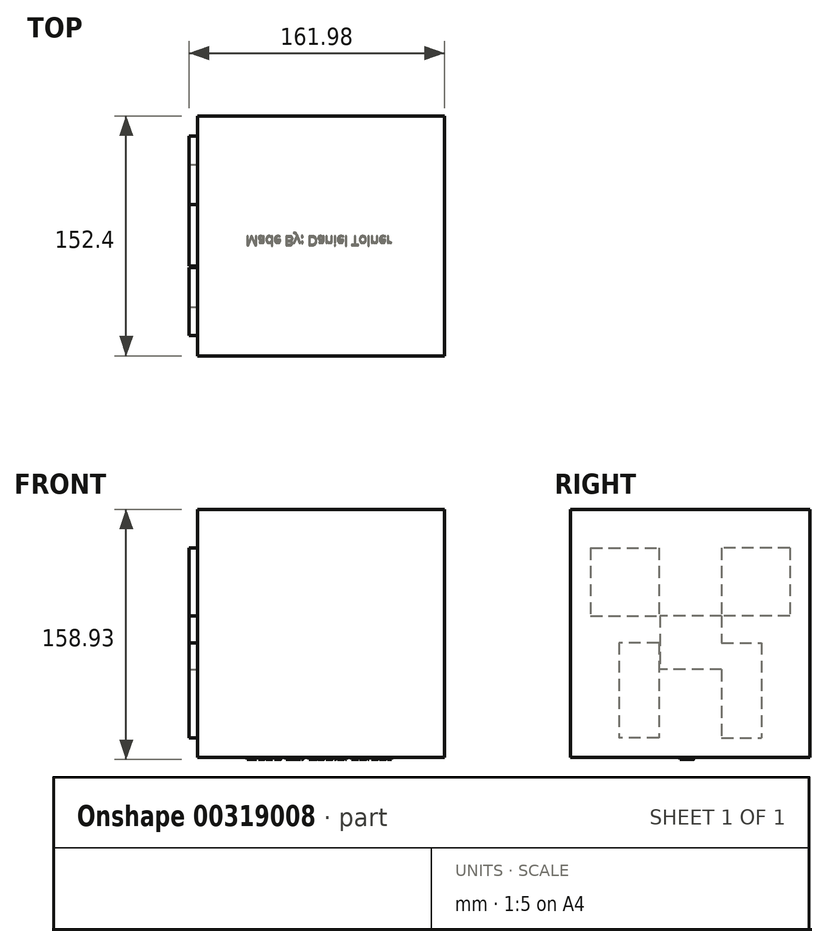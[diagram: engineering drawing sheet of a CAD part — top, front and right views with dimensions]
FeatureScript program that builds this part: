
annotation { "Feature Type Name" : "Feature", "Feature Type Description" : "" }
export const myFeature = defineFeature(function(context is Context, id is Id, definition is map)
    precondition{}
    {
        {
            var Q0;
            Q0=qCreatedBy(makeId("Front.planeOp"),FACE);
            var sketch = newSketch(context, id + "F0", { "sketchPlane" : qUnion([Q0])});
            skLineSegment(sketch, "E0.bottom", {"start": v(-81, -82.02) * mm, "end": v(75.64, -82.02) * mm});
            skLineSegment(sketch, "E0.top", {"start": v(-81, 75.64) * mm, "end": v(75.64, 75.64) * mm});
            skLineSegment(sketch, "E0.left", {"start": v(-81, -82.02) * mm, "end": v(-81, 75.64) * mm});
            skLineSegment(sketch, "E0.right", {"start": v(75.64, -82.02) * mm, "end": v(75.64, 75.64) * mm});
            skSolve(sketch);
        }
        {
            var Q0;
            Q0=makeQuery(id+"F0.imprint","IMPRINT",FACE,{"disambiguationData":[TD([[makeQuery(id+"F0.imprint","IMPRINT",EDGE,{"derivedFrom":sQuery(id+"F0.wireOp",EDGE,"E0.bottom")}),1.0]])]});
            extrude(context, id + "F1", {"entities" : qUnion([Q0]), "endBound" : BoundingType.SYMMETRIC, "depth" : 152.4 * mm});
        }
        {
            var Q0;
            Q0=makeQuery(id+"F1.opExtrude","SWEPT_FACE",FACE,{"disambiguationData":[OSD([sQuery(id+"F0.wireOp",EDGE,"E0.left")])]});
            var sketch = newSketch(context, id + "F2", { "sketchPlane" : qUnion([Q0])});
            skLineSegment(sketch, "E1.bottom", {"start": v(-63.3, 51.08) * mm, "end": v(-19.95, 51.08) * mm});
            skLineSegment(sketch, "E1.top", {"start": v(-63.3, 8.01) * mm, "end": v(-19.95, 8.01) * mm});
            skLineSegment(sketch, "E1.left", {"start": v(-63.3, 51.08) * mm, "end": v(-63.3, 8.01) * mm});
            skLineSegment(sketch, "E1.right", {"start": v(-19.95, 51.08) * mm, "end": v(-19.95, 8.01) * mm});
            skLineSegment(sketch, "E2.bottom", {"start": v(-19.95, 8.01) * mm, "end": v(19.3, 8.01) * mm});
            skLineSegment(sketch, "E2.top", {"start": v(-19.95, -26.17) * mm, "end": v(19.3, -26.17) * mm});
            skLineSegment(sketch, "E2.left", {"start": v(-19.95, 8.01) * mm, "end": v(-19.95, -26.17) * mm});
            skLineSegment(sketch, "E2.right", {"start": v(19.3, 8.01) * mm, "end": v(19.3, -26.17) * mm});
            skLineSegment(sketch, "E3.bottom", {"start": v(-19.95, -9.08) * mm, "end": v(-45.28, -9.08) * mm});
            skLineSegment(sketch, "E3.top", {"start": v(-19.95, -69.55) * mm, "end": v(-45.28, -69.55) * mm});
            skLineSegment(sketch, "E3.left", {"start": v(-19.95, -9.08) * mm, "end": v(-19.95, -69.55) * mm});
            skLineSegment(sketch, "E3.right", {"start": v(-45.28, -9.08) * mm, "end": v(-45.28, -69.55) * mm});
            skLineSegment(sketch, "E4.MirrorCS", {"start": v(19.95, 51.08) * mm, "end": v(19.95, 8.01) * mm});
            skLineSegment(sketch, "E5.MirrorCS", {"start": v(63.3, 51.08) * mm, "end": v(63.3, 8.01) * mm});
            skLineSegment(sketch, "E6.MirrorCS", {"start": v(19.95, 8.01) * mm, "end": v(19.95, -26.17) * mm});
            skLineSegment(sketch, "E7.MirrorCS", {"start": v(63.3, 51.08) * mm, "end": v(19.95, 51.08) * mm});
            skLineSegment(sketch, "E8.MirrorCS", {"start": v(63.3, 8.01) * mm, "end": v(19.95, 8.01) * mm});
            skLineSegment(sketch, "E9.MirrorCS", {"start": v(19.95, -9.08) * mm, "end": v(45.28, -9.08) * mm});
            skLineSegment(sketch, "E10.MirrorCS", {"start": v(19.95, -69.55) * mm, "end": v(45.28, -69.55) * mm});
            skLineSegment(sketch, "E11.MirrorCS", {"start": v(45.28, -9.08) * mm, "end": v(45.28, -69.55) * mm});
            skLineSegment(sketch, "E12.MirrorCS", {"start": v(19.95, -9.08) * mm, "end": v(19.95, -69.55) * mm});
            skSolve(sketch);
        }
        {
            var Q0;
            Q0 = qSketchRegion(id + "F2", true);
            extrude(context, id + "F3", {"entities" : qUnion([Q0]), "depth" : 5.33 * mm});
        }
        {
            var Q0;
            Q0=makeQuery(id+"F1.opExtrude","SWEPT_FACE",FACE,{"disambiguationData":[OSD([sQuery(id+"F0.wireOp",EDGE,"E0.bottom")])]});
            var sketch = newSketch(context, id + "F4", { "sketchPlane" : qUnion([Q0])});
            skText(sketch, "E13", { "text": "Made By: Daniel Tolner", "fontName": "OpenSans-Regular.ttf"});
            const initialGuessF4  = {"E13": [-0.05057, 0, 1, 0, 0.0062]};
            skSetInitialGuess(sketch, initialGuessF4);
            skSolve(sketch);
        }
        {
            var Q0;
            Q0 = qSketchRegion(id + "F4", true);
            extrude(context, id + "F5", {"entities" : qUnion([Q0]), "operationType" : NewBodyOperationType.ADD, "depth" : 1.27 * mm});
        }
    });
